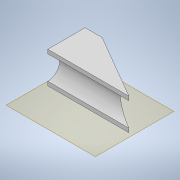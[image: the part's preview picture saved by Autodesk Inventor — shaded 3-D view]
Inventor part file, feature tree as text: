
AUTODESK INVENTOR PART (.ipt)
format: ipt  version: 2022.3 (Build 263350000, 350)  size: 117,760 bytes
history: native  units: mm
features: extrude x3, sketch x3, other x2, plane x1, reference x1
ambient origin geometry x8: Origin, YZ Plane, XZ Plane, XY Plane, X Axis, Y Axis, Z Axis, Center Point
bodies: Solid1 (feature_tree)
feature tree (10):
  plane  "Work Plane1"
  extrude  "Extrusion1"  Depth=8.0mm
  extrude  "Extrusion2"  TaperAngle=0.0deg  [1 undecoded]
  extrude  "Extrusion3"  [1 undecoded]
  sketch  "Sketch1"  dims[d0=8.0mm d1=0.0mm d2=6.0mm]
  reference  "Reference1"
  sketch  "Sketch2"  dims[d3=15.981mm d4=0.0mm d9=0.0mm d10=0.0mm]
  sketch  "Sketch3"
  other  "v2.0.iam"
  other  "Base:1"
note: 2 required parameter values undecoded (feature->parameter linkage not recoverable at this tier; creation-order binding heuristic only, values carry confidence <= 0.55)
